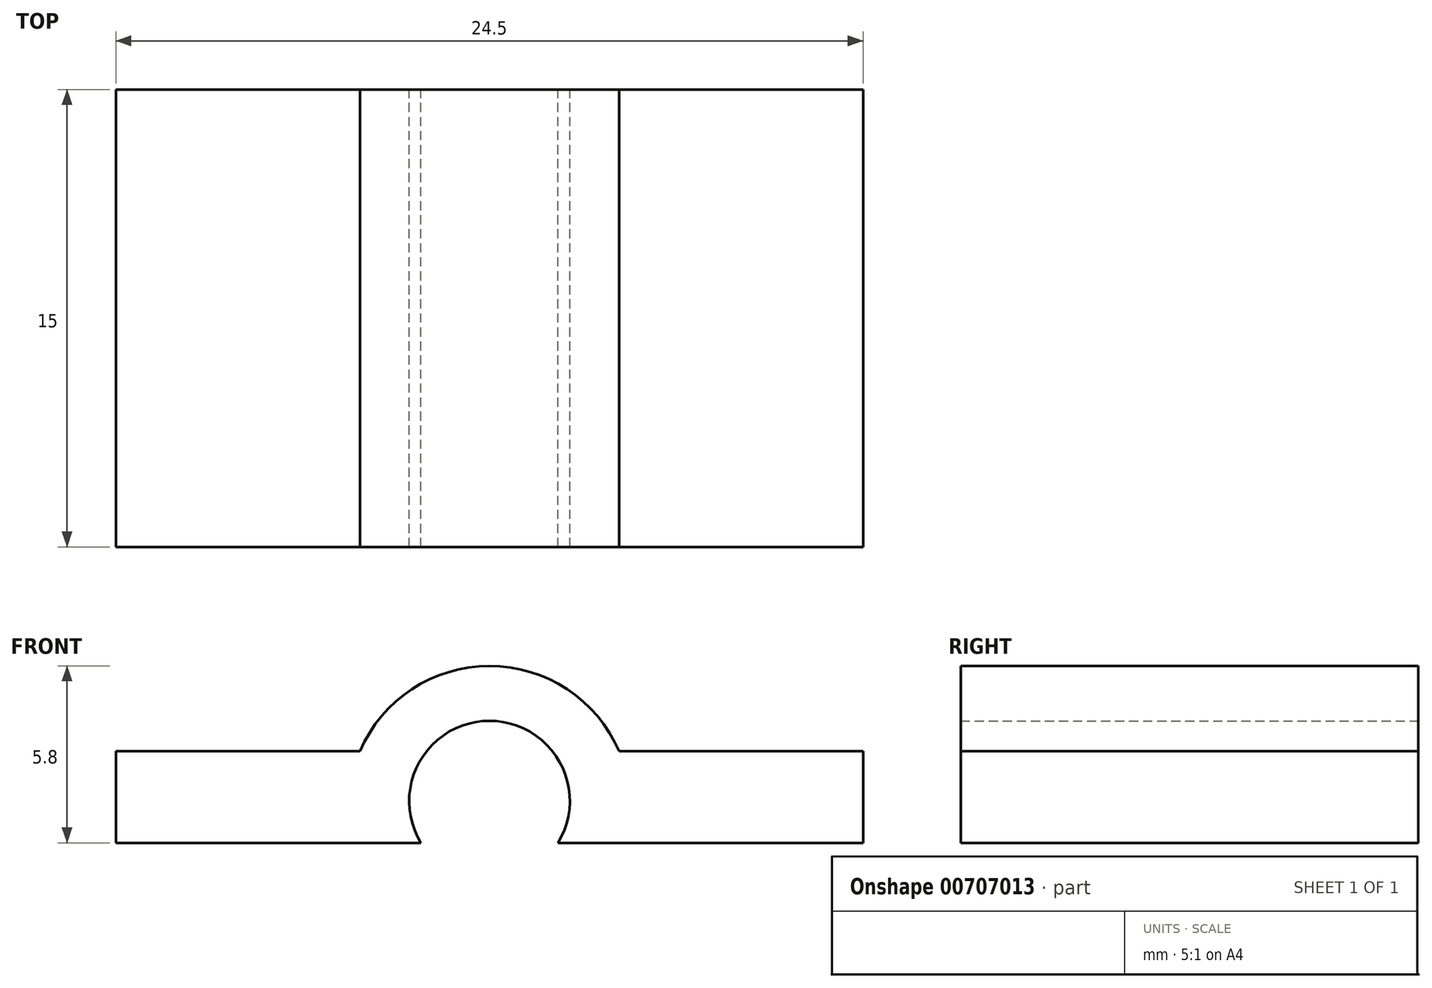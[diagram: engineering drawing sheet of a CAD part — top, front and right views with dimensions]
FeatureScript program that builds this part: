
annotation { "Feature Type Name" : "Feature", "Feature Type Description" : "" }
export const myFeature = defineFeature(function(context is Context, id is Id, definition is map)
    precondition{}
    {
        {
            var Q0;
            Q0=qCreatedBy(makeId("Front.planeOp"),FACE);
            var sketch = newSketch(context, id + "F0", { "sketchPlane" : qUnion([Q0])});
            skLineSegment(sketch, "E0", {"start": v(-12.25, 0) * mm, "end": v(-2.25, 0) * mm});
            skLineSegment(sketch, "E1", {"start": v(-12.25, 0) * mm, "end": v(-12.25, 3) * mm});
            skLineSegment(sketch, "E2", {"start": v(-12.25, 3) * mm, "end": v(-4.25, 3) * mm});
            skLineSegment(sketch, "E3", {"start": v(4.25, 3) * mm, "end": v(12.25, 3) * mm});
            skLineSegment(sketch, "E4", {"start": v(12.25, 3) * mm, "end": v(12.25, 0) * mm});
            skLineSegment(sketch, "E5", {"start": v(12.25, 0) * mm, "end": v(2.25, 0) * mm});
            skArc(sketch, "E6", {"start": v(4.25, 3) * mm, "mid": v(0, 5.8) * mm, "end": v(-4.25, 3) * mm});
            skArc(sketch, "E7", {"start": v(2.25, 0) * mm, "mid": v(0, 4) * mm, "end": v(-2.25, 0) * mm});
            skLineSegment(sketch, "E8", {"start": v(0, 1.37) * mm, "end": v(0, 0) * mm, "construction": true});
            skSolve(sketch);
        }
        {
            var Q0;
            Q0=makeQuery(id+"F0.imprint","IMPRINT",FACE,{"disambiguationData":[TD([[makeQuery(id+"F0.imprint","IMPRINT",EDGE,{"derivedFrom":sQuery(id+"F0.wireOp",EDGE,"E0")}),1.0]])]});
            extrude(context, id + "F1", {"entities" : qUnion([Q0]), "depth" : 15 * mm, "offsetDistance" : 25 * mm});
        }
    });
